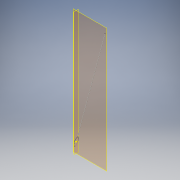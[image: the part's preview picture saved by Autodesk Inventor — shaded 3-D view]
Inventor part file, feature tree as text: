
AUTODESK INVENTOR PART (.ipt)
format: ipt  version: 2016 (Build 200138000, 138)  size: 193,536 bytes
history: native  units: in
note: dims shown in document units (in); Inventor stores cm internally (conversion verified against a paired STEP export)
features: sketch x6, plane x3, extrude x2, sweep x1
ambient origin geometry x8: Origin, YZ Plane, XZ Plane, XY Plane, X Axis, Y Axis, Z Axis, Center Point
bodies: Solid1 (feature_tree)
feature tree (12):
  plane  "Work Plane1"
  plane  "Work Plane2"
  sketch  "Sketch1"  dims[d0=-0.1031in d1=75.0deg d2=2.9528in]
  sketch  "Sketch3"  dims[d3=0.2362in d4=0.0in d5=0.0in]
  sketch  "Sketch4"  dims[d6=0.2362in d7=70.8661in d8=0.0in]
  sweep  "Sweep1"
  extrude  "Extrusion1"  TaperAngle=0.0deg  [1 undecoded]
  plane  "Work Plane3"
  extrude  "Extrusion2"  Depth=70.8661in TaperAngle=0.0deg
  sketch  "Sketch5"  dims[d9=70.8661in d10=0.0in]
  sketch  "Sketch6"
  sketch  "Sketch7"
note: 1 required parameter value undecoded (feature->parameter linkage not recoverable at this tier; creation-order binding heuristic only, values carry confidence <= 0.55)
